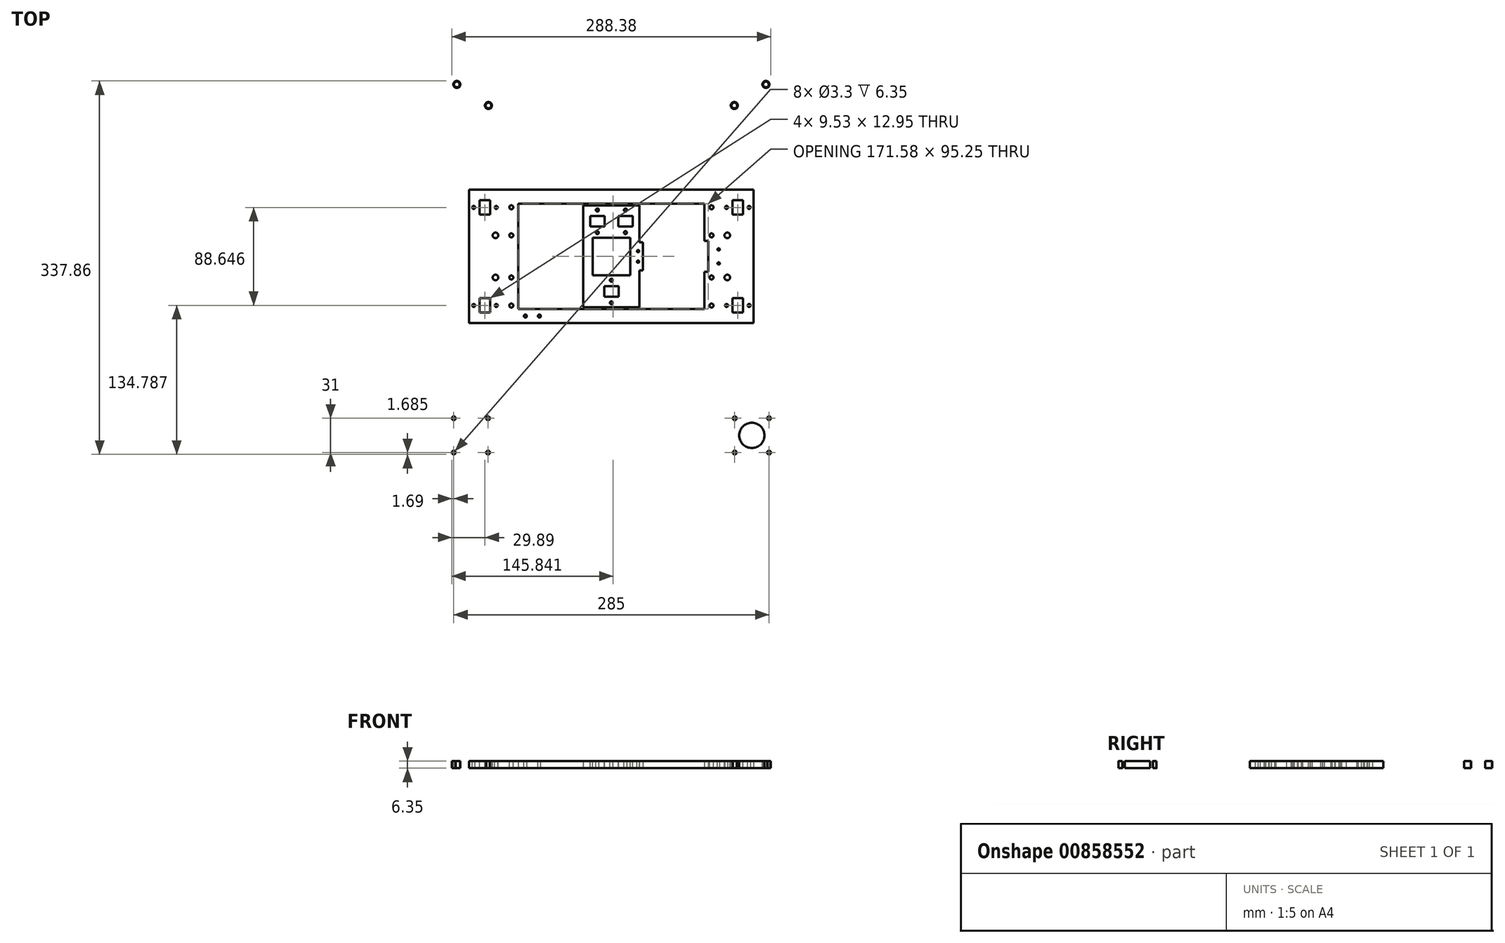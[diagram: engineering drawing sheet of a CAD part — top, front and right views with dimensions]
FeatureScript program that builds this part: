
annotation { "Feature Type Name" : "Feature", "Feature Type Description" : "" }
export const myFeature = defineFeature(function(context is Context, id is Id, definition is map)
    precondition{}
    {
        {
            var Q0;
            Q0=qCreatedBy(makeId("Top.planeOp"),FACE);
            var sketch = newSketch(context, id + "F0", { "sketchPlane" : qUnion([Q0])});
            skLineSegment(sketch, "E0.bottom", {"start": v(25.4, 46.04) * mm, "end": v(-25.4, 46.04) * mm});
            skLineSegment(sketch, "E0.top", {"start": v(25.4, -46.04) * mm, "end": v(-25.4, -46.04) * mm});
            skLineSegment(sketch, "E0.left", {"start": v(25.4, 46.04) * mm, "end": v(25.4, -46.04) * mm});
            skLineSegment(sketch, "E0.right", {"start": v(-25.4, 46.04) * mm, "end": v(-25.4, -46.04) * mm});
            skPoint(sketch, "E0.middle", {"position": v(0, 0) * mm});
            skLineSegment(sketch, "E1.bottom", {"start": v(128.59, 60.33) * mm, "end": v(-128.59, 60.32) * mm});
            skLineSegment(sketch, "E1.top", {"start": v(128.59, -60.32) * mm, "end": v(-128.59, -60.33) * mm});
            skLineSegment(sketch, "E1.left", {"start": v(128.59, 60.33) * mm, "end": v(128.59, -60.32) * mm});
            skLineSegment(sketch, "E1.right", {"start": v(-128.59, 60.32) * mm, "end": v(-128.59, -60.33) * mm});
            skLineSegment(sketch, "E2.0", {"start": v(84.14, 47.63) * mm, "end": v(-84.14, 47.62) * mm});
            skLineSegment(sketch, "E3.0", {"start": v(84.14, -47.62) * mm, "end": v(-84.14, -47.63) * mm});
            skLineSegment(sketch, "E4.trimOffspring", {"start": v(-84.14, 47.62) * mm, "end": v(-84.14, -47.63) * mm});
            skLineSegment(sketch, "E5.trimOffspring", {"start": v(84.14, 47.62) * mm, "end": v(84.14, -47.62) * mm});
            skLineSegment(sketch, "E6.bottom", {"start": v(-131.76, 120.65) * mm, "end": v(131.76, 120.65) * mm});
            skLineSegment(sketch, "E6.top", {"start": v(-131.76, -120.65) * mm, "end": v(131.76, -120.65) * mm});
            skLineSegment(sketch, "E6.left", {"start": v(-131.76, 120.65) * mm, "end": v(-131.76, -120.65) * mm});
            skLineSegment(sketch, "E6.right", {"start": v(131.76, 120.65) * mm, "end": v(131.76, -120.65) * mm});
            skLineSegment(sketch, "E7.bottom", {"start": v(-177.8, 168.28) * mm, "end": v(177.8, 168.28) * mm});
            skLineSegment(sketch, "E7.top", {"start": v(-177.8, -168.28) * mm, "end": v(177.8, -168.28) * mm});
            skLineSegment(sketch, "E7.left", {"start": v(-177.8, 168.28) * mm, "end": v(-177.8, -187.33) * mm});
            skLineSegment(sketch, "E7.right", {"start": v(177.8, 168.28) * mm, "end": v(177.8, -187.33) * mm});
            skLineSegment(sketch, "E8.0", {"start": v(-177.8, -187.33) * mm, "end": v(177.8, -187.33) * mm});
            skLineSegment(sketch, "E9.bottom", {"start": v(28.58, 12.7) * mm, "end": v(22.23, 12.7) * mm});
            skLineSegment(sketch, "E9.top", {"start": v(28.58, -12.7) * mm, "end": v(22.23, -12.7) * mm});
            skLineSegment(sketch, "E9.left", {"start": v(28.58, 12.7) * mm, "end": v(28.58, -12.7) * mm});
            skLineSegment(sketch, "E9.right", {"start": v(22.23, 12.7) * mm, "end": v(22.23, -12.7) * mm});
            skPoint(sketch, "E9.middle", {"position": v(25.4, 0) * mm});
            skLineSegment(sketch, "E10.bottom", {"start": v(87.44, 13.97) * mm, "end": v(80.84, 13.97) * mm});
            skLineSegment(sketch, "E10.top", {"start": v(87.44, -13.97) * mm, "end": v(80.84, -13.97) * mm});
            skLineSegment(sketch, "E10.left", {"start": v(87.44, 13.97) * mm, "end": v(87.44, -13.97) * mm});
            skLineSegment(sketch, "E10.right", {"start": v(80.84, 13.97) * mm, "end": v(80.84, -13.97) * mm});
            skPoint(sketch, "E10.middle", {"position": v(84.14, 0) * mm});
            skSolve(sketch);
        }
        {
            var Q0;
            Q0=makeQuery(id+"F0.imprint","IMPRINT",FACE,{"disambiguationData":[TD([[makeQuery(id+"F0.imprint","IMPRINT",EDGE,{"derivedFrom":sQuery(id+"F0.wireOp",EDGE,"E1.bottom")}),1.0]])]});
            extrude(context, id + "F1", {"entities" : qUnion([Q0]), "depth" : 6.35 * mm, "offsetDistance" : 25.4 * mm});
        }
        {
            var Q0;
            Q0=makeQuery(id+"F0.imprint","IMPRINT",FACE,{"disambiguationData":[TD([[makeQuery(id+"F0.imprint","IMPRINT",EDGE,{"derivedFrom":sQuery(id+"F0.wireOp",EDGE,"E0.bottom")}),1.0]])]});
            var Q1;
            {var subQ5=sQuery(id+"F0.wireOp",EDGE,"E9.right");Q1=makeQuery(id+"F0.imprint","IMPRINT",FACE,{"disambiguationData":[TD([[makeQuery(id+"F0.imprint","IMPRINT",EDGE,{"derivedFrom":subQ5}),1.0]])]});}
            var Q2;
            {var subQ5=sQuery(id+"F0.wireOp",EDGE,"E9.left");Q2=makeQuery(id+"F0.imprint","IMPRINT",FACE,{"disambiguationData":[TD([[makeQuery(id+"F0.imprint","IMPRINT",EDGE,{"derivedFrom":subQ5}),-1.0]])]});}
            extrude(context, id + "F2", {"entities" : qUnion([Q0, Q1, Q2]), "depth" : 6.35 * mm, "offsetDistance" : 25.4 * mm});
        }
        {
            var Q0;
            Q0=makeQuery(id+"F0.imprint","IMPRINT",FACE,{"disambiguationData":[TD([[makeQuery(id+"F0.imprint","IMPRINT",EDGE,{"derivedFrom":sQuery(id+"F0.wireOp",EDGE,"E6.bottom")}),1.0]])]});
            var Q1;
            {var subQ0=sQuery(id+"F0.wireOp",EDGE,"E7.top");Q1=makeQuery(id+"F0.imprint","IMPRINT",FACE,{"disambiguationData":[TD([[makeQuery(id+"F0.imprint","IMPRINT",EDGE,{"derivedFrom":subQ0}),-1.0]])]});}
            extrude(context, id + "F3", {"entities" : qUnion([Q0, Q1]), "depth" : 6.35 * mm, "offsetDistance" : 25.4 * mm});
        }
        {
            var Q0;
            Q0=makeQuery(id+"F3.opExtrude","CAP_FACE",FACE,{"disambiguationData":[OSD([sQuery(id+"F0.wireOp",EDGE,"E6.bottom"),sQuery(id+"F0.wireOp",EDGE,"E6.top"),sQuery(id+"F0.wireOp",EDGE,"E6.left"),sQuery(id+"F0.wireOp",EDGE,"E6.right"),sQuery(id+"F0.wireOp",EDGE,"E7.bottom"),sQuery(id+"F0.wireOp",EDGE,"E7.left"),sQuery(id+"F0.wireOp",EDGE,"E7.right"),sQuery(id+"F0.wireOp",EDGE,"E8.0")])],"isStart":false});
            var sketch = newSketch(context, id + "F4", { "sketchPlane" : qUnion([Q0])});
            skCircle(sketch, "E11", {"center": v(-127, -161.93) * mm, "radius": 11.43 * mm});
            skCircle(sketch, "E12", {"center": v(-111.5, -146.43) * mm, "radius": 1.69 * mm});
            skCircle(sketch, "E13.1.0", {"center": v(-142.5, -146.43) * mm, "radius": 1.69 * mm});
            skCircle(sketch, "E13.2.0", {"center": v(-142.5, -177.42) * mm, "radius": 1.69 * mm});
            skCircle(sketch, "E13.3.0", {"center": v(-111.5, -177.43) * mm, "radius": 1.69 * mm});
            skLineSegment(sketch, "E14", {"start": v(0, -187.33) * mm, "end": v(0, 168.28) * mm, "construction": true});
            skPoint(sketch, "E15.MirrorP", {"position": v(127, -161.93) * mm});
            skCircle(sketch, "E16.MirrorC", {"center": v(111.5, -146.43) * mm, "radius": 1.69 * mm});
            skCircle(sketch, "E17.MirrorC", {"center": v(142.5, -146.43) * mm, "radius": 1.69 * mm});
            skCircle(sketch, "E18.MirrorC", {"center": v(142.5, -177.42) * mm, "radius": 1.69 * mm});
            skCircle(sketch, "E19.MirrorC", {"center": v(111.5, -177.43) * mm, "radius": 1.69 * mm});
            skCircle(sketch, "E20.MirrorC", {"center": v(127, -161.93) * mm, "radius": 11.43 * mm});
            skCircle(sketch, "E21", {"center": v(-139.7, 155.58) * mm, "radius": 3.18 * mm});
            skCircle(sketch, "E22", {"center": v(-111.12, 136.53) * mm, "radius": 3.18 * mm});
            skCircle(sketch, "E23.MirrorC", {"center": v(111.12, 136.53) * mm, "radius": 3.18 * mm});
            skCircle(sketch, "E24.MirrorC", {"center": v(139.7, 155.58) * mm, "radius": 3.18 * mm});
            skSolve(sketch);
        }
        {
            var Q0;
            Q0=makeQuery(id+"F4.imprint","IMPRINT",FACE,{"disambiguationData":[TD([[makeQuery(id+"F4.imprint","IMPRINT",EDGE,{"derivedFrom":sQuery(id+"F4.wireOp",EDGE,"E11")}),1.0]])]});
            var Q1;
            Q1=makeQuery(id+"F4.imprint","IMPRINT",FACE,{"disambiguationData":[TD([[makeQuery(id+"F4.imprint","IMPRINT",EDGE,{"derivedFrom":sQuery(id+"F4.wireOp",EDGE,"E20.MirrorC")}),-1.0]])]});
            var Q2;
            Q2=sQuery(id+"F0.wireOp",EDGE,"E6.top");
            var Q3;
            Q3=sQuery(id+"F0.wireOp",EDGE,"E8.0");
            var Q4;
            Q4=sQuery(id+"F4.wireOp",EDGE,"E11");
            extrude(context, id + "F5", {"entities" : qUnion([Q0, Q1]), "operationType" : NewBodyOperationType.REMOVE, "surfaceEntities" : qUnion([Q2, Q3, Q4]), "oppositeDirection" : true, "depth" : 25.4 * mm, "offsetDistance" : 25.4 * mm});
        }
        {
            var Q0;
            Q0=sQuery(id+"F4.wireOp",VERTEX,"E13.1.0.center");
            var Q1;
            Q1=sQuery(id+"F4.wireOp",VERTEX,"E12.center");
            var Q2;
            Q2=sQuery(id+"F4.wireOp",VERTEX,"E13.3.0.center");
            var Q3;
            Q3=sQuery(id+"F4.wireOp",VERTEX,"E13.2.0.center");
            var Q4;
            Q4=sQuery(id+"F4.wireOp",VERTEX,"E16.MirrorC.center");
            var Q5;
            Q5=sQuery(id+"F4.wireOp",VERTEX,"E17.MirrorC.center");
            var Q6;
            Q6=sQuery(id+"F4.wireOp",VERTEX,"E19.MirrorC.center");
            var Q7;
            Q7=sQuery(id+"F4.wireOp",VERTEX,"E18.MirrorC.center");
            var Q8;
            Q8=makeQuery(id+"F3.opExtrude","SWEPT_BODY",BODY,{"disambiguationData":[OSD([sQuery(id+"F0.wireOp",EDGE,"E6.bottom"),sQuery(id+"F0.wireOp",EDGE,"E6.top"),sQuery(id+"F0.wireOp",EDGE,"E6.left"),sQuery(id+"F0.wireOp",EDGE,"E6.right"),sQuery(id+"F0.wireOp",EDGE,"E7.bottom"),sQuery(id+"F0.wireOp",EDGE,"E7.left"),sQuery(id+"F0.wireOp",EDGE,"E7.right"),sQuery(id+"F0.wireOp",EDGE,"E8.0")])]});
            hole(context, id + "F6", {"style" : HoleStyle.SIMPLE, "endStyle" : HoleEndStyle.THROUGH, "standardTappedOrClearance" : lookupTablePath({ "fit" : "Normal", "standard" : "ISO", "size" : "M3", "type" : "Clearance" }), "standardBlindInLast" : lookupTablePath({ "fit" : "Standard", "standard" : "ISO", "size" : "M3", "type" : "Clearance" }), "holeDiameter" : 3.3 * mm, "majorDiameter" : 6.35 * mm, "isTappedThrough" : true, "tappedDepth" : 12.7 * mm, "tapClearance" : 3, "locations" : qUnion([Q0, Q1, Q2, Q3, Q4, Q5, Q6, Q7]), "scope" : qUnion([Q8])});
        }
        {
            var Q0;
            Q0=makeQuery(id+"F4.imprint","IMPRINT",FACE,{"disambiguationData":[TD([[makeQuery(id+"F4.imprint","IMPRINT",EDGE,{"derivedFrom":makeQuery(id+"F3.opExtrude","CAP_EDGE",EDGE,{"disambiguationData":[OSD([sQuery(id+"F0.wireOp",EDGE,"E6.bottom")])],"isStart":false})}),-1.0]])]});
            var sketch = newSketch(context, id + "F7", { "sketchPlane" : qUnion([Q0])});
            skLineSegment(sketch, "E25.bottom", {"start": v(-119.06, 50.8) * mm, "end": v(-109.54, 50.8) * mm});
            skLineSegment(sketch, "E25.top", {"start": v(-119.06, 37.85) * mm, "end": v(-109.54, 37.85) * mm});
            skLineSegment(sketch, "E25.left", {"start": v(-119.06, 50.8) * mm, "end": v(-119.06, 37.85) * mm});
            skLineSegment(sketch, "E25.right", {"start": v(-109.54, 50.8) * mm, "end": v(-109.54, 37.85) * mm});
            skLineSegment(sketch, "E26.MirrorCS", {"start": v(109.54, 50.8) * mm, "end": v(109.54, 37.85) * mm});
            skLineSegment(sketch, "E27.MirrorCS", {"start": v(119.06, 50.8) * mm, "end": v(119.06, 37.85) * mm});
            skLineSegment(sketch, "E28.MirrorCS", {"start": v(119.06, 37.85) * mm, "end": v(109.54, 37.85) * mm});
            skLineSegment(sketch, "E29.MirrorCS", {"start": v(119.06, 50.8) * mm, "end": v(109.54, 50.8) * mm});
            skLineSegment(sketch, "E30", {"start": v(-183.3, 0) * mm, "end": v(191.16, 0) * mm, "construction": true});
            skLineSegment(sketch, "E31.MirrorCS", {"start": v(-119.06, -37.85) * mm, "end": v(-109.54, -37.85) * mm});
            skLineSegment(sketch, "E32.MirrorCS", {"start": v(-119.06, -50.8) * mm, "end": v(-109.54, -50.8) * mm});
            skLineSegment(sketch, "E33.MirrorCS", {"start": v(-109.54, -50.8) * mm, "end": v(-109.54, -37.85) * mm});
            skLineSegment(sketch, "E34.MirrorCS", {"start": v(-119.06, -50.8) * mm, "end": v(-119.06, -37.85) * mm});
            skLineSegment(sketch, "E35.MirrorCS", {"start": v(119.06, -50.8) * mm, "end": v(109.54, -50.8) * mm});
            skLineSegment(sketch, "E36.MirrorCS", {"start": v(119.06, -37.85) * mm, "end": v(109.54, -37.85) * mm});
            skLineSegment(sketch, "E37.MirrorCS", {"start": v(119.06, -50.8) * mm, "end": v(119.06, -37.85) * mm});
            skLineSegment(sketch, "E38.MirrorCS", {"start": v(109.54, -50.8) * mm, "end": v(109.54, -37.85) * mm});
            skLineSegment(sketch, "E39.bottom", {"start": v(-19.18, 36.51) * mm, "end": v(-6.22, 36.51) * mm});
            skLineSegment(sketch, "E39.top", {"start": v(-19.18, 26.99) * mm, "end": v(-6.22, 26.99) * mm});
            skLineSegment(sketch, "E39.left", {"start": v(-19.18, 36.51) * mm, "end": v(-19.18, 26.99) * mm});
            skLineSegment(sketch, "E39.right", {"start": v(-6.22, 36.51) * mm, "end": v(-6.22, 26.99) * mm});
            skLineSegment(sketch, "E40", {"start": v(-12.7, 36.51) * mm, "end": v(-12.7, 26.99) * mm, "construction": true});
            skLineSegment(sketch, "E41.bottom", {"start": v(-6.48, -26.99) * mm, "end": v(6.48, -26.99) * mm});
            skLineSegment(sketch, "E41.top", {"start": v(-6.48, -36.51) * mm, "end": v(6.48, -36.51) * mm});
            skLineSegment(sketch, "E41.left", {"start": v(-6.48, -26.99) * mm, "end": v(-6.48, -36.51) * mm});
            skLineSegment(sketch, "E41.right", {"start": v(6.48, -26.99) * mm, "end": v(6.48, -36.51) * mm});
            skLineSegment(sketch, "E42", {"start": v(0, -26.99) * mm, "end": v(0, -36.51) * mm, "construction": true});
            skLineSegment(sketch, "E43.MirrorCS", {"start": v(19.18, 36.51) * mm, "end": v(19.18, 26.99) * mm});
            skLineSegment(sketch, "E44.MirrorCS", {"start": v(19.18, 36.51) * mm, "end": v(6.22, 36.51) * mm});
            skLineSegment(sketch, "E45.MirrorCS", {"start": v(19.18, 26.99) * mm, "end": v(6.22, 26.99) * mm});
            skLineSegment(sketch, "E46.MirrorCS", {"start": v(12.7, 36.51) * mm, "end": v(12.7, 26.99) * mm, "construction": true});
            skLineSegment(sketch, "E47.MirrorCS", {"start": v(6.22, 36.51) * mm, "end": v(6.22, 26.99) * mm});
            skCircle(sketch, "E48", {"center": v(-104.08, 44.32) * mm, "radius": 1.59 * mm});
            skPoint(sketch, "E48.centerSnap0", {"position": v(-109.54, 44.32) * mm});
            skCircle(sketch, "E49", {"center": v(-124.52, 44.32) * mm, "radius": 1.59 * mm});
            skPoint(sketch, "E49.centerSnap0", {"position": v(-119.06, 44.32) * mm});
            skLineSegment(sketch, "E50", {"start": v(-114.3, 50.8) * mm, "end": v(-114.3, 37.85) * mm, "construction": true});
            skCircle(sketch, "E51.MirrorC", {"center": v(104.08, 44.32) * mm, "radius": 1.59 * mm});
            skCircle(sketch, "E52.MirrorC", {"center": v(124.52, 44.32) * mm, "radius": 1.59 * mm});
            skCircle(sketch, "E53.MirrorC", {"center": v(104.08, -44.32) * mm, "radius": 1.59 * mm});
            skCircle(sketch, "E54.MirrorC", {"center": v(124.52, -44.32) * mm, "radius": 1.59 * mm});
            skCircle(sketch, "E55.MirrorC", {"center": v(-104.08, -44.32) * mm, "radius": 1.59 * mm});
            skCircle(sketch, "E56.MirrorC", {"center": v(-124.52, -44.32) * mm, "radius": 1.59 * mm});
            skCircle(sketch, "E57", {"center": v(-12.7, 41.97) * mm, "radius": 1.59 * mm});
            skCircle(sketch, "E58", {"center": v(-12.7, 21.53) * mm, "radius": 1.59 * mm});
            skLineSegment(sketch, "E59", {"start": v(-97, 31.75) * mm, "end": v(-6.22, 31.75) * mm, "construction": true});
            skCircle(sketch, "E60", {"center": v(0, -21.53) * mm, "radius": 1.59 * mm});
            skCircle(sketch, "E61", {"center": v(0, -41.97) * mm, "radius": 1.59 * mm});
            skLineSegment(sketch, "E62", {"start": v(-6.48, -31.75) * mm, "end": v(6.48, -31.75) * mm, "construction": true});
            skCircle(sketch, "E63.MirrorC", {"center": v(12.7, 41.97) * mm, "radius": 1.59 * mm});
            skCircle(sketch, "E64.MirrorC", {"center": v(12.7, 21.53) * mm, "radius": 1.59 * mm});
            skPoint(sketch, "E65.orphan", {"position": v(-19.18, 31.75) * mm});
            skCircle(sketch, "E66", {"center": v(-90.49, 44.45) * mm, "radius": 1.59 * mm});
            skCircle(sketch, "E67.MirrorC", {"center": v(-90.49, 19.05) * mm, "radius": 1.59 * mm});
            skCircle(sketch, "E68.MirrorC", {"center": v(-90.49, -19.05) * mm, "radius": 1.59 * mm});
            skCircle(sketch, "E69.MirrorC", {"center": v(-90.49, -44.45) * mm, "radius": 1.59 * mm});
            skCircle(sketch, "E70.MirrorC", {"center": v(90.49, 44.45) * mm, "radius": 1.59 * mm});
            skCircle(sketch, "E71.MirrorC", {"center": v(90.49, 19.05) * mm, "radius": 1.59 * mm});
            skCircle(sketch, "E72.MirrorC", {"center": v(90.49, -19.05) * mm, "radius": 1.59 * mm});
            skCircle(sketch, "E73.MirrorC", {"center": v(90.49, -44.45) * mm, "radius": 1.59 * mm});
            skCircle(sketch, "E74", {"center": v(-104.78, -19.05) * mm, "radius": 3.18 * mm});
            skCircle(sketch, "E75.MirrorC", {"center": v(-104.78, 19.05) * mm, "radius": 3.18 * mm});
            skCircle(sketch, "E76.MirrorC", {"center": v(104.78, 19.05) * mm, "radius": 3.18 * mm});
            skCircle(sketch, "E77.MirrorC", {"center": v(104.78, -19.05) * mm, "radius": 3.18 * mm});
            skLineSegment(sketch, "E78.bottom", {"start": v(-17, 17) * mm, "end": v(17, 17) * mm});
            skLineSegment(sketch, "E78.top", {"start": v(-17, -17) * mm, "end": v(17, -17) * mm});
            skLineSegment(sketch, "E78.left", {"start": v(-17, 17) * mm, "end": v(-17, -17) * mm});
            skLineSegment(sketch, "E78.right", {"start": v(17, 17) * mm, "end": v(17, -17) * mm});
            skPoint(sketch, "E78.middle", {"position": v(0, 0) * mm});
            skCircle(sketch, "E79", {"center": v(-77.79, -53.98) * mm, "radius": 1.59 * mm});
            skCircle(sketch, "E80", {"center": v(-65.09, -53.98) * mm, "radius": 1.59 * mm});
            skLineSegment(sketch, "E81", {"start": v(-77.79, -53.98) * mm, "end": v(-65.09, -53.98) * mm, "construction": true});
            skLineSegment(sketch, "E82", {"start": v(-71.44, -53.98) * mm, "end": v(-71.44, -139.5) * mm, "construction": true});
            skCircle(sketch, "E83", {"center": v(-76.19, -129.86) * mm, "radius": 1.59 * mm});
            skCircle(sketch, "E84.MirrorC", {"center": v(-66.69, -129.86) * mm, "radius": 1.59 * mm});
            skCircle(sketch, "E85", {"center": v(24.13, 4.75) * mm, "radius": 1.59 * mm});
            skCircle(sketch, "E86.MirrorC", {"center": v(24.13, -4.75) * mm, "radius": 1.59 * mm});
            skCircle(sketch, "E87", {"center": v(96.96, 6.35) * mm, "radius": 1.59 * mm});
            skCircle(sketch, "E88.MirrorC", {"center": v(96.96, -6.35) * mm, "radius": 1.59 * mm});
            skSolve(sketch);
        }
        {
            var Q0;
            Q0=makeQuery(id+"F7.imprint","IMPRINT",FACE,{"disambiguationData":[TD([[makeQuery(id+"F7.imprint","IMPRINT",EDGE,{"derivedFrom":sQuery(id+"F7.wireOp",EDGE,"E31.MirrorCS")}),-1.0]])]});
            var Q1;
            Q1=makeQuery(id+"F7.imprint","IMPRINT",FACE,{"disambiguationData":[TD([[makeQuery(id+"F7.imprint","IMPRINT",EDGE,{"derivedFrom":sQuery(id+"F7.wireOp",EDGE,"E25.bottom")}),-1.0]])]});
            var Q2;
            Q2=makeQuery(id+"F7.imprint","IMPRINT",FACE,{"disambiguationData":[TD([[makeQuery(id+"F7.imprint","IMPRINT",EDGE,{"derivedFrom":sQuery(id+"F7.wireOp",EDGE,"E39.bottom")}),-1.0]])]});
            var Q3;
            Q3=makeQuery(id+"F7.imprint","IMPRINT",FACE,{"disambiguationData":[TD([[makeQuery(id+"F7.imprint","IMPRINT",EDGE,{"derivedFrom":sQuery(id+"F7.wireOp",EDGE,"E35.MirrorCS")}),-1.0]])]});
            var Q4;
            Q4=makeQuery(id+"F7.imprint","IMPRINT",FACE,{"disambiguationData":[TD([[makeQuery(id+"F7.imprint","IMPRINT",EDGE,{"derivedFrom":sQuery(id+"F7.wireOp",EDGE,"E26.MirrorCS")}),1.0]])]});
            var Q5;
            Q5=makeQuery(id+"F7.imprint","IMPRINT",FACE,{"disambiguationData":[TD([[makeQuery(id+"F7.imprint","IMPRINT",EDGE,{"derivedFrom":sQuery(id+"F7.wireOp",EDGE,"E41.bottom")}),-1.0]])]});
            var Q6;
            Q6=makeQuery(id+"F7.imprint","IMPRINT",FACE,{"disambiguationData":[TD([[makeQuery(id+"F7.imprint","IMPRINT",EDGE,{"derivedFrom":sQuery(id+"F7.wireOp",EDGE,"E43.MirrorCS")}),-1.0]])]});
            var Q7;
            Q7=makeQuery(id+"F7.imprint","IMPRINT",FACE,{"disambiguationData":[TD([[makeQuery(id+"F7.imprint","IMPRINT",EDGE,{"derivedFrom":sQuery(id+"F7.wireOp",EDGE,"E78.bottom")}),-1.0]])]});
            extrude(context, id + "F8", {"entities" : qUnion([Q0, Q1, Q2, Q3, Q4, Q5, Q6, Q7]), "operationType" : NewBodyOperationType.REMOVE, "oppositeDirection" : true, "depth" : 25.4 * mm, "offsetDistance" : 25.4 * mm});
        }
        {
            var Q0;
            Q0=sQuery(id+"F7.wireOp",VERTEX,"E49.center");
            var Q1;
            Q1=sQuery(id+"F7.wireOp",VERTEX,"E48.center");
            var Q2;
            Q2=sQuery(id+"F7.wireOp",VERTEX,"E56.MirrorC.center");
            var Q3;
            Q3=sQuery(id+"F7.wireOp",VERTEX,"E55.MirrorC.center");
            var Q4;
            Q4=sQuery(id+"F7.wireOp",VERTEX,"E58.center");
            var Q5;
            Q5=sQuery(id+"F7.wireOp",VERTEX,"E57.center");
            var Q6;
            Q6=sQuery(id+"F7.wireOp",VERTEX,"E63.MirrorC.center");
            var Q7;
            Q7=sQuery(id+"F7.wireOp",VERTEX,"E64.MirrorC.center");
            var Q8;
            Q8=sQuery(id+"F7.wireOp",VERTEX,"E60.center");
            var Q9;
            Q9=sQuery(id+"F7.wireOp",VERTEX,"E61.center");
            var Q10;
            Q10=sQuery(id+"F7.wireOp",VERTEX,"E51.MirrorC.center");
            var Q11;
            Q11=sQuery(id+"F7.wireOp",VERTEX,"E52.MirrorC.center");
            var Q12;
            Q12=sQuery(id+"F7.wireOp",VERTEX,"E53.MirrorC.center");
            var Q13;
            Q13=sQuery(id+"F7.wireOp",VERTEX,"E54.MirrorC.center");
            var Q14;
            Q14=sQuery(id+"F7.wireOp",VERTEX,"E79.center");
            var Q15;
            Q15=sQuery(id+"F7.wireOp",VERTEX,"E80.center");
            var Q16;
            Q16=makeQuery(id+"F1.opExtrude","SWEPT_BODY",BODY,{"disambiguationData":[OSD([sQuery(id+"F0.wireOp",EDGE,"E1.bottom"),sQuery(id+"F0.wireOp",EDGE,"E1.top"),sQuery(id+"F0.wireOp",EDGE,"E1.left"),sQuery(id+"F0.wireOp",EDGE,"E1.right"),sQuery(id+"F0.wireOp",EDGE,"E2.0"),sQuery(id+"F0.wireOp",EDGE,"E3.0"),sQuery(id+"F0.wireOp",EDGE,"E4.trimOffspring"),sQuery(id+"F0.wireOp",EDGE,"E5.trimOffspring")])]});
            var Q17;
            Q17=makeQuery(id+"F2.opExtrude","SWEPT_BODY",BODY,{"disambiguationData":[OSD([sQuery(id+"F0.wireOp",EDGE,"E0.bottom"),sQuery(id+"F0.wireOp",EDGE,"E0.top"),sQuery(id+"F0.wireOp",EDGE,"E0.left"),sQuery(id+"F0.wireOp",EDGE,"E0.right")])]});
            hole(context, id + "F9", {"style" : HoleStyle.SIMPLE, "endStyle" : HoleEndStyle.THROUGH, "standardTappedOrClearance" : lookupTablePath({ "standard" : "ANSI", "engagement" : "75%", "pitch" : "32 tpi", "size" : "#6", "type" : "Tapped" }), "standardBlindInLast" : lookupTablePath({ "standard" : "ANSI", "engagement" : "75%", "pitch" : "32 tpi", "size" : "#6", "type" : "Tapped" }), "holeDiameter" : 2.7 * mm, "majorDiameter" : 3.5 * mm, "showTappedDepth" : true, "isTappedThrough" : true, "tappedDepth" : 12.7 * mm, "tapClearance" : 3, "locations" : qUnion([Q0, Q1, Q2, Q3, Q4, Q5, Q6, Q7, Q8, Q9, Q10, Q11, Q12, Q13, Q14, Q15]), "scope" : qUnion([Q16, Q17])});
        }
        {
            var Q0;
            Q0=makeQuery(id+"F4.imprint","IMPRINT",FACE,{"disambiguationData":[TD([[makeQuery(id+"F4.imprint","IMPRINT",EDGE,{"derivedFrom":sQuery(id+"F4.wireOp",EDGE,"E11")}),-1.0]])]});
            var sketch = newSketch(context, id + "F10", { "sketchPlane" : qUnion([Q0])});
            skLineSegment(sketch, "E89", {"start": v(-114.3, -154.76) * mm, "end": v(-114.3, -50.8) * mm, "construction": true});
            skCircle(sketch, "E90", {"center": v(-127, -127) * mm, "radius": 1.59 * mm});
            skCircle(sketch, "E91.MirrorC", {"center": v(-101.6, -127) * mm, "radius": 1.59 * mm});
            skLineSegment(sketch, "E92", {"start": v(-131.76, 0) * mm, "end": v(134.96, 0) * mm, "construction": true});
            skCircle(sketch, "E93.MirrorC", {"center": v(-101.6, 127) * mm, "radius": 1.59 * mm});
            skCircle(sketch, "E94.MirrorC", {"center": v(-127, 127) * mm, "radius": 1.59 * mm});
            skCircle(sketch, "E95.MirrorC", {"center": v(101.6, -127) * mm, "radius": 1.59 * mm});
            skCircle(sketch, "E96.MirrorC", {"center": v(127, -127) * mm, "radius": 1.59 * mm});
            skCircle(sketch, "E97.MirrorC", {"center": v(101.6, 127) * mm, "radius": 1.59 * mm});
            skCircle(sketch, "E98.MirrorC", {"center": v(127, 127) * mm, "radius": 1.59 * mm});
            skSolve(sketch);
        }
        {
            var Q0;
            Q0=sQuery(id+"F10.wireOp",VERTEX,"E90.center");
            var Q1;
            Q1=sQuery(id+"F10.wireOp",VERTEX,"E91.MirrorC.center");
            var Q2;
            Q2=sQuery(id+"F7.wireOp",VERTEX,"E66.center");
            var Q3;
            Q3=sQuery(id+"F7.wireOp",VERTEX,"E67.MirrorC.center");
            var Q4;
            Q4=sQuery(id+"F10.wireOp",VERTEX,"E94.MirrorC.center");
            var Q5;
            Q5=sQuery(id+"F10.wireOp",VERTEX,"E93.MirrorC.center");
            var Q6;
            Q6=sQuery(id+"F10.wireOp",VERTEX,"E97.MirrorC.center");
            var Q7;
            Q7=sQuery(id+"F10.wireOp",VERTEX,"E98.MirrorC.center");
            var Q8;
            Q8=sQuery(id+"F10.wireOp",VERTEX,"E96.MirrorC.center");
            var Q9;
            Q9=sQuery(id+"F10.wireOp",VERTEX,"E95.MirrorC.center");
            var Q10;
            Q10=sQuery(id+"F7.wireOp",VERTEX,"E68.MirrorC.center");
            var Q11;
            Q11=sQuery(id+"F7.wireOp",VERTEX,"E69.MirrorC.center");
            var Q12;
            Q12=sQuery(id+"F7.wireOp",VERTEX,"E73.MirrorC.center");
            var Q13;
            Q13=sQuery(id+"F7.wireOp",VERTEX,"E72.MirrorC.center");
            var Q14;
            Q14=sQuery(id+"F7.wireOp",VERTEX,"E71.MirrorC.center");
            var Q15;
            Q15=sQuery(id+"F7.wireOp",VERTEX,"E70.MirrorC.center");
            var Q16;
            Q16=makeQuery(id+"F3.opExtrude","SWEPT_BODY",BODY,{"disambiguationData":[OSD([sQuery(id+"F0.wireOp",EDGE,"E6.bottom"),sQuery(id+"F0.wireOp",EDGE,"E6.top"),sQuery(id+"F0.wireOp",EDGE,"E6.left"),sQuery(id+"F0.wireOp",EDGE,"E6.right"),sQuery(id+"F0.wireOp",EDGE,"E7.bottom"),sQuery(id+"F0.wireOp",EDGE,"E7.left"),sQuery(id+"F0.wireOp",EDGE,"E7.right"),sQuery(id+"F0.wireOp",EDGE,"E8.0")])]});
            var Q17;
            Q17=makeQuery(id+"F1.opExtrude","SWEPT_BODY",BODY,{"disambiguationData":[OSD([sQuery(id+"F0.wireOp",EDGE,"E1.bottom"),sQuery(id+"F0.wireOp",EDGE,"E1.top"),sQuery(id+"F0.wireOp",EDGE,"E1.left"),sQuery(id+"F0.wireOp",EDGE,"E1.right"),sQuery(id+"F0.wireOp",EDGE,"E2.0"),sQuery(id+"F0.wireOp",EDGE,"E3.0"),sQuery(id+"F0.wireOp",EDGE,"E4.trimOffspring"),sQuery(id+"F0.wireOp",EDGE,"E5.trimOffspring")])]});
            hole(context, id + "F11", {"style" : HoleStyle.SIMPLE, "endStyle" : HoleEndStyle.THROUGH, "standardTappedOrClearance" : lookupTablePath({ "fit" : "Close", "standard" : "ANSI", "size" : "#6", "type" : "Clearance" }), "standardBlindInLast" : lookupTablePath({ "fit" : "Close", "standard" : "ANSI", "size" : "#6", "type" : "Clearance" }), "holeDiameter" : 3.66 * mm, "majorDiameter" : 6.35 * mm, "isTappedThrough" : true, "tappedDepth" : 12.7 * mm, "tapClearance" : 3, "locations" : qUnion([Q0, Q1, Q2, Q3, Q4, Q5, Q6, Q7, Q8, Q9, Q10, Q11, Q12, Q13, Q14, Q15]), "scope" : qUnion([Q16, Q17])});
        }
        {
            var Q0;
            Q0=sQuery(id+"F7.wireOp",VERTEX,"E83.center");
            var Q1;
            Q1=sQuery(id+"F7.wireOp",VERTEX,"E84.MirrorC.center");
            var Q2;
            Q2=sQuery(id+"F7.wireOp",VERTEX,"E87.center");
            var Q3;
            Q3=sQuery(id+"F7.wireOp",VERTEX,"E88.MirrorC.center");
            var Q4;
            Q4=makeQuery(id+"F3.opExtrude","SWEPT_BODY",BODY,{"disambiguationData":[OSD([sQuery(id+"F0.wireOp",EDGE,"E6.bottom"),sQuery(id+"F0.wireOp",EDGE,"E6.top"),sQuery(id+"F0.wireOp",EDGE,"E6.left"),sQuery(id+"F0.wireOp",EDGE,"E6.right"),sQuery(id+"F0.wireOp",EDGE,"E7.bottom"),sQuery(id+"F0.wireOp",EDGE,"E7.left"),sQuery(id+"F0.wireOp",EDGE,"E7.right"),sQuery(id+"F0.wireOp",EDGE,"E8.0")])]});
            var Q5;
            Q5=makeQuery(id+"F1.opExtrude","SWEPT_BODY",BODY,{"disambiguationData":[OSD([sQuery(id+"F0.wireOp",EDGE,"E1.bottom"),sQuery(id+"F0.wireOp",EDGE,"E1.top"),sQuery(id+"F0.wireOp",EDGE,"E1.left"),sQuery(id+"F0.wireOp",EDGE,"E1.right"),sQuery(id+"F0.wireOp",EDGE,"E2.0"),sQuery(id+"F0.wireOp",EDGE,"E3.0"),sQuery(id+"F0.wireOp",EDGE,"E4.trimOffspring"),sQuery(id+"F0.wireOp",EDGE,"E5.trimOffspring"),sQuery(id+"F0.wireOp",EDGE,"E10.bottom"),sQuery(id+"F0.wireOp",EDGE,"E10.top"),sQuery(id+"F0.wireOp",EDGE,"E10.left")])]});
            hole(context, id + "F12", {"style" : HoleStyle.SIMPLE, "endStyle" : HoleEndStyle.THROUGH, "standardTappedOrClearance" : lookupTablePath({ "standard" : "ANSI", "engagement" : "75%", "pitch" : "56 tpi", "size" : "#3", "type" : "Tapped" }), "standardBlindInLast" : lookupTablePath({ "standard" : "ANSI", "engagement" : "75%", "pitch" : "56 tpi", "size" : "#3", "type" : "Tapped" }), "holeDiameter" : 2.08 * mm, "majorDiameter" : 2.5 * mm, "showTappedDepth" : true, "isTappedThrough" : true, "tappedDepth" : 12.7 * mm, "tapClearance" : 3, "locations" : qUnion([Q0, Q1, Q2, Q3]), "scope" : qUnion([Q4, Q5])});
        }
        {
            var Q0;
            Q0=sQuery(id+"F7.wireOp",VERTEX,"E85.center");
            var Q1;
            Q1=sQuery(id+"F7.wireOp",VERTEX,"E86.MirrorC.center");
            var Q2;
            Q2=makeQuery(id+"F2.opExtrude","SWEPT_BODY",BODY,{"disambiguationData":[OSD([sQuery(id+"F0.wireOp",EDGE,"E0.bottom"),sQuery(id+"F0.wireOp",EDGE,"E0.top"),sQuery(id+"F0.wireOp",EDGE,"E0.left"),sQuery(id+"F0.wireOp",EDGE,"E0.right"),sQuery(id+"F0.wireOp",EDGE,"E9.bottom"),sQuery(id+"F0.wireOp",EDGE,"E9.top"),sQuery(id+"F0.wireOp",EDGE,"E9.left")])]});
            hole(context, id + "F13", {"style" : HoleStyle.SIMPLE, "endStyle" : HoleEndStyle.THROUGH, "standardTappedOrClearance" : lookupTablePath({ "standard" : "ANSI", "engagement" : "75%", "pitch" : "56 tpi", "size" : "#3", "type" : "Tapped" }), "standardBlindInLast" : lookupTablePath({ "standard" : "ANSI", "engagement" : "75%", "pitch" : "56 tpi", "size" : "#3", "type" : "Tapped" }), "holeDiameter" : 2.08 * mm, "majorDiameter" : 2.5 * mm, "showTappedDepth" : true, "isTappedThrough" : true, "tappedDepth" : 12.7 * mm, "tapClearance" : 3, "locations" : qUnion([Q0, Q1]), "scope" : qUnion([Q2])});
        }
        {
            var Q0;
            Q0=sQuery(id+"F7.wireOp",VERTEX,"E75.MirrorC.center");
            var Q1;
            Q1=sQuery(id+"F7.wireOp",VERTEX,"E74.center");
            var Q2;
            Q2=sQuery(id+"F7.wireOp",VERTEX,"E77.MirrorC.center");
            var Q3;
            Q3=sQuery(id+"F7.wireOp",VERTEX,"E76.MirrorC.center");
            var Q4;
            Q4=makeQuery(id+"F1.opExtrude","SWEPT_BODY",BODY,{"disambiguationData":[OSD([sQuery(id+"F0.wireOp",EDGE,"E1.bottom"),sQuery(id+"F0.wireOp",EDGE,"E1.top"),sQuery(id+"F0.wireOp",EDGE,"E1.left"),sQuery(id+"F0.wireOp",EDGE,"E1.right"),sQuery(id+"F0.wireOp",EDGE,"E2.0"),sQuery(id+"F0.wireOp",EDGE,"E3.0"),sQuery(id+"F0.wireOp",EDGE,"E4.trimOffspring"),sQuery(id+"F0.wireOp",EDGE,"E5.trimOffspring"),sQuery(id+"F0.wireOp",EDGE,"E10.bottom"),sQuery(id+"F0.wireOp",EDGE,"E10.top"),sQuery(id+"F0.wireOp",EDGE,"E10.left")])]});
            var Q5;
            Q5=makeQuery(id+"F3.opExtrude","SWEPT_BODY",BODY,{"disambiguationData":[OSD([sQuery(id+"F0.wireOp",EDGE,"E6.bottom"),sQuery(id+"F0.wireOp",EDGE,"E6.top"),sQuery(id+"F0.wireOp",EDGE,"E6.left"),sQuery(id+"F0.wireOp",EDGE,"E6.right"),sQuery(id+"F0.wireOp",EDGE,"E7.bottom"),sQuery(id+"F0.wireOp",EDGE,"E7.left"),sQuery(id+"F0.wireOp",EDGE,"E7.right"),sQuery(id+"F0.wireOp",EDGE,"E8.0")])]});
            hole(context, id + "F14", {"style" : HoleStyle.SIMPLE, "endStyle" : HoleEndStyle.THROUGH, "standardTappedOrClearance" : lookupTablePath({ "standard" : "ANSI", "engagement" : "75%", "pitch" : "20 tpi", "size" : "1/4", "type" : "Tapped" }), "standardBlindInLast" : lookupTablePath({ "standard" : "ANSI", "engagement" : "75%", "pitch" : "20 tpi", "size" : "1/4", "type" : "Tapped" }), "holeDiameter" : 5.1 * mm, "majorDiameter" : 6.35 * mm, "showTappedDepth" : true, "isTappedThrough" : true, "tappedDepth" : 12.7 * mm, "tapClearance" : 3, "locations" : qUnion([Q0, Q1, Q2, Q3]), "scope" : qUnion([Q4, Q5])});
        }
        {
            var Q0;
            Q0=sQuery(id+"F4.wireOp",VERTEX,"E21.center");
            var Q1;
            Q1=sQuery(id+"F4.wireOp",VERTEX,"E22.center");
            var Q2;
            Q2=sQuery(id+"F4.wireOp",VERTEX,"E23.MirrorC.center");
            var Q3;
            Q3=sQuery(id+"F4.wireOp",VERTEX,"E24.MirrorC.center");
            var Q4;
            Q4=makeQuery(id+"F3.opExtrude","SWEPT_BODY",BODY,{"disambiguationData":[OSD([sQuery(id+"F0.wireOp",EDGE,"E6.bottom"),sQuery(id+"F0.wireOp",EDGE,"E6.top"),sQuery(id+"F0.wireOp",EDGE,"E6.left"),sQuery(id+"F0.wireOp",EDGE,"E6.right"),sQuery(id+"F0.wireOp",EDGE,"E7.bottom"),sQuery(id+"F0.wireOp",EDGE,"E7.left"),sQuery(id+"F0.wireOp",EDGE,"E7.right"),sQuery(id+"F0.wireOp",EDGE,"E8.0")])]});
            hole(context, id + "F15", {"style" : HoleStyle.SIMPLE, "endStyle" : HoleEndStyle.THROUGH, "standardTappedOrClearance" : lookupTablePath({ "standard" : "ANSI", "engagement" : "75%", "pitch" : "20 tpi", "size" : "1/4", "type" : "Tapped" }), "standardBlindInLast" : lookupTablePath({ "standard" : "ANSI", "engagement" : "75%", "pitch" : "20 tpi", "size" : "1/4", "type" : "Tapped" }), "holeDiameter" : 5.1 * mm, "majorDiameter" : 6.35 * mm, "showTappedDepth" : true, "isTappedThrough" : true, "tappedDepth" : 12.7 * mm, "tapClearance" : 3, "locations" : qUnion([Q0, Q1, Q2, Q3]), "scope" : qUnion([Q4])});
        }
    });
